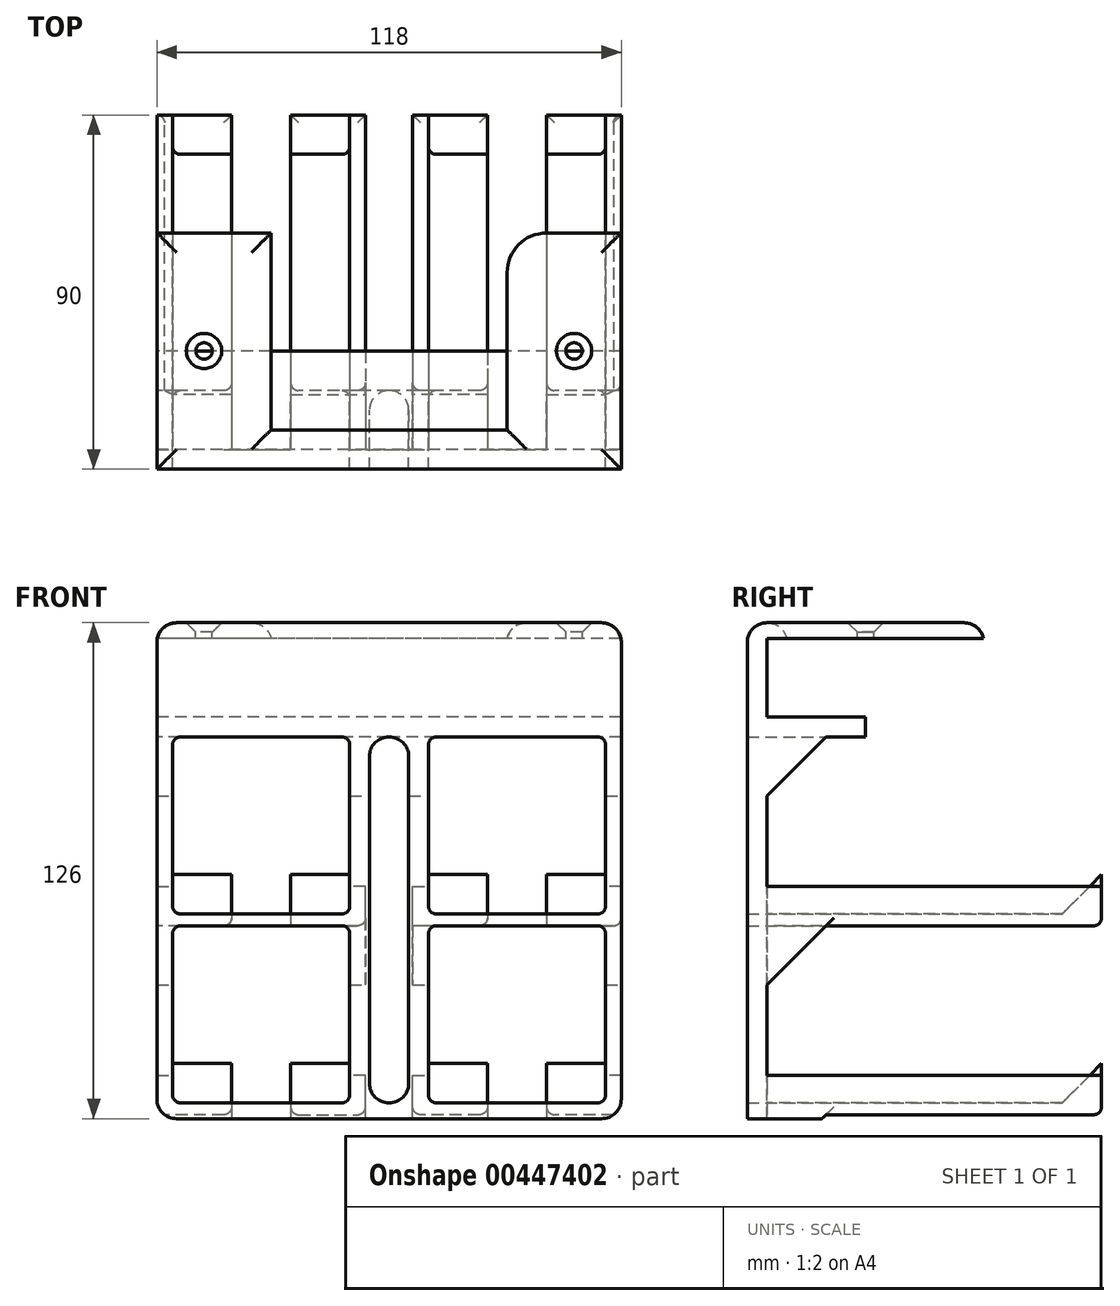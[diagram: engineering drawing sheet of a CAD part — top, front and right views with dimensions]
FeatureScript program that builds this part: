
annotation { "Feature Type Name" : "Feature", "Feature Type Description" : "" }
export const myFeature = defineFeature(function(context is Context, id is Id, definition is map)
    precondition{}
    {
        {
            var Q0;
            Q0=qCreatedBy(makeId("Front.planeOp"),FACE);
            var sketch = newSketch(context, id + "F0", { "sketchPlane" : qUnion([Q0])});
            skLineSegment(sketch, "E0.bottom", {"start": v(-55, -29) * mm, "end": v(-10, -29) * mm});
            skLineSegment(sketch, "E0.top", {"start": v(-55, -74) * mm, "end": v(-10, -74) * mm});
            skLineSegment(sketch, "E0.left", {"start": v(-55, -29) * mm, "end": v(-55, -74) * mm});
            skLineSegment(sketch, "E0.right", {"start": v(-10, -29) * mm, "end": v(-10, -74) * mm});
            skLineSegment(sketch, "E1.MirrorCS", {"start": v(10, -29) * mm, "end": v(10, -74) * mm});
            skLineSegment(sketch, "E2.MirrorCS", {"start": v(55, -29) * mm, "end": v(55, -74) * mm});
            skLineSegment(sketch, "E3.MirrorCS", {"start": v(55, -29) * mm, "end": v(10, -29) * mm});
            skLineSegment(sketch, "E4.MirrorCS", {"start": v(55, -74) * mm, "end": v(10, -74) * mm});
            skLineSegment(sketch, "E5", {"start": v(-55, -75.5) * mm, "end": v(55, -75.5) * mm, "construction": true});
            skLineSegment(sketch, "E6.MirrorCS", {"start": v(-55, -77) * mm, "end": v(-10, -77) * mm});
            skLineSegment(sketch, "E7.MirrorCS", {"start": v(-55, -122) * mm, "end": v(-55, -77) * mm});
            skLineSegment(sketch, "E8.MirrorCS", {"start": v(-55, -122) * mm, "end": v(-10, -122) * mm});
            skLineSegment(sketch, "E9.MirrorCS", {"start": v(-10, -122) * mm, "end": v(-10, -77) * mm});
            skLineSegment(sketch, "E10.MirrorCS", {"start": v(10, -122) * mm, "end": v(10, -77) * mm});
            skLineSegment(sketch, "E11.MirrorCS", {"start": v(55, -122) * mm, "end": v(10, -122) * mm});
            skLineSegment(sketch, "E12.MirrorCS", {"start": v(55, -122) * mm, "end": v(55, -77) * mm});
            skLineSegment(sketch, "E13.MirrorCS", {"start": v(55, -77) * mm, "end": v(10, -77) * mm});
            skLineSegment(sketch, "E14.bottom", {"start": v(-59, 0) * mm, "end": v(59, 0) * mm});
            skLineSegment(sketch, "E14.top", {"start": v(-59, -126) * mm, "end": v(59, -126) * mm});
            skLineSegment(sketch, "E14.left", {"start": v(-59, 0) * mm, "end": v(-59, -126) * mm});
            skLineSegment(sketch, "E14.right", {"start": v(59, 0) * mm, "end": v(59, -126) * mm});
            skLineSegment(sketch, "E15", {"start": v(0, -34) * mm, "end": v(0, -117) * mm, "construction": true});
            skLineSegment(sketch, "E16", {"start": v(0, -117) * mm, "end": v(0, -122) * mm, "construction": true});
            skLineSegment(sketch, "E17", {"start": v(0, -34) * mm, "end": v(0, -29) * mm, "construction": true});
            skArc(sketch, "E18.0.startCap", {"start": v(-5, -34) * mm, "mid": v(0, -29) * mm, "end": v(5, -34) * mm});
            skArc(sketch, "E18.0.endCap", {"start": v(5, -117) * mm, "mid": v(0, -122) * mm, "end": v(-5, -117) * mm});
            skLineSegment(sketch, "E18.0.left", {"start": v(5, -34) * mm, "end": v(5, -117) * mm});
            skLineSegment(sketch, "E18.0.right", {"start": v(-5, -34) * mm, "end": v(-5, -117) * mm});
            skSolve(sketch);
        }
        {
            var Q0;
            Q0=makeQuery(id+"F0.imprint","IMPRINT",FACE,{"disambiguationData":[TD([[makeQuery(id+"F0.imprint","IMPRINT",EDGE,{"derivedFrom":sQuery(id+"F0.wireOp",EDGE,"E0.bottom")}),1.0]])]});
            extrude(context, id + "F1", {"entities" : qUnion([Q0]), "depth" : 5 * mm});
        }
        {
            var Q0;
            Q0=makeQuery(id+"F1.opExtrude","CAP_FACE",FACE,{"disambiguationData":[OSD([sQuery(id+"F0.wireOp",EDGE,"E0.bottom"),sQuery(id+"F0.wireOp",EDGE,"E0.top"),sQuery(id+"F0.wireOp",EDGE,"E0.left"),sQuery(id+"F0.wireOp",EDGE,"E0.right"),sQuery(id+"F0.wireOp",EDGE,"E1.MirrorCS"),sQuery(id+"F0.wireOp",EDGE,"E2.MirrorCS"),sQuery(id+"F0.wireOp",EDGE,"E3.MirrorCS"),sQuery(id+"F0.wireOp",EDGE,"E4.MirrorCS"),sQuery(id+"F0.wireOp",EDGE,"E6.MirrorCS"),sQuery(id+"F0.wireOp",EDGE,"E7.MirrorCS"),sQuery(id+"F0.wireOp",EDGE,"E8.MirrorCS"),sQuery(id+"F0.wireOp",EDGE,"E9.MirrorCS"),sQuery(id+"F0.wireOp",EDGE,"E10.MirrorCS"),sQuery(id+"F0.wireOp",EDGE,"E11.MirrorCS"),sQuery(id+"F0.wireOp",EDGE,"E12.MirrorCS"),sQuery(id+"F0.wireOp",EDGE,"E13.MirrorCS"),sQuery(id+"F0.wireOp",EDGE,"E14.bottom"),sQuery(id+"F0.wireOp",EDGE,"E14.top"),sQuery(id+"F0.wireOp",EDGE,"E14.left"),sQuery(id+"F0.wireOp",EDGE,"E14.right")])],"isStart":true});
            var sketch = newSketch(context, id + "F2", { "sketchPlane" : qUnion([Q0])});
            skLineSegment(sketch, "E19.bottom", {"start": v(-59, 0) * mm, "end": v(59, 0) * mm});
            skLineSegment(sketch, "E19.top", {"start": v(-59, -4) * mm, "end": v(59, -4) * mm});
            skLineSegment(sketch, "E19.left", {"start": v(-59, 0) * mm, "end": v(-59, -4) * mm});
            skLineSegment(sketch, "E19.right", {"start": v(59, 0) * mm, "end": v(59, -4) * mm});
            skSolve(sketch);
        }
        {
            var Q0;
            Q0 = qSketchRegion(id + "F2", true);
            extrude(context, id + "F3", {"entities" : qUnion([Q0]), "operationType" : NewBodyOperationType.ADD, "depth" : 55 * mm});
        }
        {
            var Q0;
            Q0=makeQuery(id+"F1.opExtrude","CAP_FACE",FACE,{"disambiguationData":[OSD([sQuery(id+"F0.wireOp",EDGE,"E0.bottom"),sQuery(id+"F0.wireOp",EDGE,"E0.top"),sQuery(id+"F0.wireOp",EDGE,"E0.left"),sQuery(id+"F0.wireOp",EDGE,"E0.right"),sQuery(id+"F0.wireOp",EDGE,"E1.MirrorCS"),sQuery(id+"F0.wireOp",EDGE,"E2.MirrorCS"),sQuery(id+"F0.wireOp",EDGE,"E3.MirrorCS"),sQuery(id+"F0.wireOp",EDGE,"E4.MirrorCS"),sQuery(id+"F0.wireOp",EDGE,"E6.MirrorCS"),sQuery(id+"F0.wireOp",EDGE,"E7.MirrorCS"),sQuery(id+"F0.wireOp",EDGE,"E8.MirrorCS"),sQuery(id+"F0.wireOp",EDGE,"E9.MirrorCS"),sQuery(id+"F0.wireOp",EDGE,"E10.MirrorCS"),sQuery(id+"F0.wireOp",EDGE,"E11.MirrorCS"),sQuery(id+"F0.wireOp",EDGE,"E12.MirrorCS"),sQuery(id+"F0.wireOp",EDGE,"E13.MirrorCS"),sQuery(id+"F0.wireOp",EDGE,"E14.bottom"),sQuery(id+"F0.wireOp",EDGE,"E14.top"),sQuery(id+"F0.wireOp",EDGE,"E14.left"),sQuery(id+"F0.wireOp",EDGE,"E14.right")])],"isStart":true});
            var sketch = newSketch(context, id + "F4", { "sketchPlane" : qUnion([Q0])});
            skLineSegment(sketch, "E20.bottom", {"start": v(-59, -24) * mm, "end": v(59, -24) * mm});
            skLineSegment(sketch, "E20.top", {"start": v(-59, -29) * mm, "end": v(59, -29) * mm});
            skLineSegment(sketch, "E20.left", {"start": v(-59, -24) * mm, "end": v(-59, -29) * mm});
            skLineSegment(sketch, "E20.right", {"start": v(59, -24) * mm, "end": v(59, -29) * mm});
            skSolve(sketch);
        }
        {
            var Q0;
            Q0=makeQuery(id+"F4.imprint","IMPRINT",FACE,{"disambiguationData":[TD([[makeQuery(id+"F4.imprint","IMPRINT",EDGE,{"derivedFrom":sQuery(id+"F4.wireOp",EDGE,"E20.bottom")}),-1.0]])]});
            extrude(context, id + "F5", {"entities" : qUnion([Q0]), "operationType" : NewBodyOperationType.ADD, "depth" : 25 * mm});
        }
        {
            var Q0;
            {var subQ0=sQuery(id+"F0.wireOp",EDGE,"E14.right");var subQ1=sQuery(id+"F0.wireOp",EDGE,"E14.left");var subQ2=sQuery(id+"F0.wireOp",EDGE,"E14.top");var subQ3=sQuery(id+"F0.wireOp",EDGE,"E13.MirrorCS");var subQ4=sQuery(id+"F0.wireOp",EDGE,"E12.MirrorCS");var subQ5=sQuery(id+"F0.wireOp",EDGE,"E11.MirrorCS");var subQ6=sQuery(id+"F0.wireOp",EDGE,"E10.MirrorCS");var subQ7=sQuery(id+"F0.wireOp",EDGE,"E9.MirrorCS");var subQ8=sQuery(id+"F0.wireOp",EDGE,"E8.MirrorCS");var subQ9=sQuery(id+"F0.wireOp",EDGE,"E0.left");var subQ10=sQuery(id+"F0.wireOp",EDGE,"E0.top");var subQ11=sQuery(id+"F0.wireOp",EDGE,"E0.right");var subQ12=sQuery(id+"F0.wireOp",EDGE,"E0.bottom");var subQ13=sQuery(id+"F0.wireOp",EDGE,"E7.MirrorCS");var subQ14=sQuery(id+"F0.wireOp",EDGE,"E1.MirrorCS");var subQ15=sQuery(id+"F0.wireOp",EDGE,"E2.MirrorCS");var subQ16=sQuery(id+"F0.wireOp",EDGE,"E3.MirrorCS");var subQ17=sQuery(id+"F0.wireOp",EDGE,"E4.MirrorCS");var subQ18=sQuery(id+"F0.wireOp",EDGE,"E6.MirrorCS");Q0=makeQuery(id+"F5.boolean.opBoolean","SPLIT",FACE,{"disambiguationData":[TD([makeQuery(id+"F1.opExtrude","SWEPT_FACE",FACE,{"disambiguationData":[OSD([subQ12])]})])],"derivedFrom":makeQuery(id+"F1.opExtrude","CAP_FACE",FACE,{"disambiguationData":[OSD([subQ12,subQ10,subQ9,subQ11,subQ14,subQ15,subQ16,subQ17,subQ18,subQ13,subQ8,subQ7,subQ6,subQ5,subQ4,subQ3,sQuery(id+"F0.wireOp",EDGE,"E14.bottom"),subQ2,subQ1,subQ0])],"isStart":true})});}
            var sketch = newSketch(context, id + "F6", { "sketchPlane" : qUnion([Q0])});
            skLineSegment(sketch, "E21", {"start": v(-59, -67) * mm, "end": v(-55, -67) * mm});
            skLineSegment(sketch, "E22", {"start": v(-55, -67) * mm, "end": v(-55, -74) * mm});
            skLineSegment(sketch, "E23", {"start": v(-55, -74) * mm, "end": v(-40, -74) * mm});
            skLineSegment(sketch, "E24", {"start": v(-40, -74) * mm, "end": v(-40, -77) * mm});
            skLineSegment(sketch, "E25", {"start": v(-40, -77) * mm, "end": v(-59, -77) * mm});
            skLineSegment(sketch, "E26", {"start": v(-59, -77) * mm, "end": v(-59, -67) * mm});
            skLineSegment(sketch, "E27", {"start": v(-32.5, -74) * mm, "end": v(-32.5, -29) * mm, "construction": true});
            skPoint(sketch, "E27.endSnap0", {"position": v(-32.5, -74) * mm});
            skLineSegment(sketch, "E28", {"start": v(5, -29) * mm, "end": v(0, -130.75) * mm, "construction": true});
            skPoint(sketch, "E28.endSnap0", {"position": v(0, -126) * mm});
            skLineSegment(sketch, "E29.MirrorCS", {"start": v(-25, -74) * mm, "end": v(-25, -77) * mm});
            skLineSegment(sketch, "E30.MirrorCS", {"start": v(-10, -74) * mm, "end": v(-25, -74) * mm});
            skLineSegment(sketch, "E31.MirrorCS", {"start": v(-25, -77) * mm, "end": v(-6, -77) * mm});
            skLineSegment(sketch, "E32.MirrorCS", {"start": v(-6, -77) * mm, "end": v(-6, -67) * mm});
            skLineSegment(sketch, "E33.MirrorCS", {"start": v(-10, -67) * mm, "end": v(-10, -74) * mm});
            skLineSegment(sketch, "E34.MirrorCS", {"start": v(-6, -67) * mm, "end": v(-10, -67) * mm});
            skLineSegment(sketch, "E35.0.1.0", {"start": v(-59, -125) * mm, "end": v(-59, -115) * mm});
            skLineSegment(sketch, "E35.0.1.1", {"start": v(-59, -115) * mm, "end": v(-55, -115) * mm});
            skLineSegment(sketch, "E35.0.1.2", {"start": v(-55, -115) * mm, "end": v(-55, -122) * mm});
            skLineSegment(sketch, "E35.0.1.3", {"start": v(-55, -122) * mm, "end": v(-40, -122) * mm});
            skLineSegment(sketch, "E35.0.1.4", {"start": v(-40, -122) * mm, "end": v(-40, -125) * mm});
            skLineSegment(sketch, "E35.0.1.5", {"start": v(-40, -125) * mm, "end": v(-59, -125) * mm});
            skLineSegment(sketch, "E35.0.1.6", {"start": v(-25, -125) * mm, "end": v(-6, -125) * mm});
            skLineSegment(sketch, "E35.0.1.7", {"start": v(-6, -125) * mm, "end": v(-6, -115) * mm});
            skLineSegment(sketch, "E35.0.1.8", {"start": v(-6, -115) * mm, "end": v(-10, -115) * mm});
            skLineSegment(sketch, "E35.0.1.9", {"start": v(-10, -115) * mm, "end": v(-10, -122) * mm});
            skLineSegment(sketch, "E35.0.1.10", {"start": v(-10, -122) * mm, "end": v(-25, -122) * mm});
            skLineSegment(sketch, "E35.0.1.11", {"start": v(-25, -122) * mm, "end": v(-25, -125) * mm});
            skLineSegment(sketch, "E35.1.0.0", {"start": v(6, -77) * mm, "end": v(6, -67) * mm});
            skLineSegment(sketch, "E35.1.0.1", {"start": v(6, -67) * mm, "end": v(10, -67) * mm});
            skLineSegment(sketch, "E35.1.0.2", {"start": v(10, -67) * mm, "end": v(10, -74) * mm});
            skLineSegment(sketch, "E35.1.0.3", {"start": v(10, -74) * mm, "end": v(25, -74) * mm});
            skLineSegment(sketch, "E35.1.0.4", {"start": v(25, -74) * mm, "end": v(25, -77) * mm});
            skLineSegment(sketch, "E35.1.0.5", {"start": v(25, -77) * mm, "end": v(6, -77) * mm});
            skLineSegment(sketch, "E35.1.0.6", {"start": v(40, -77) * mm, "end": v(59, -77) * mm});
            skLineSegment(sketch, "E35.1.0.7", {"start": v(59, -77) * mm, "end": v(59, -67) * mm});
            skLineSegment(sketch, "E35.1.0.8", {"start": v(59, -67) * mm, "end": v(55, -67) * mm});
            skLineSegment(sketch, "E35.1.0.9", {"start": v(55, -67) * mm, "end": v(55, -74) * mm});
            skLineSegment(sketch, "E35.1.0.10", {"start": v(55, -74) * mm, "end": v(40, -74) * mm});
            skLineSegment(sketch, "E35.1.0.11", {"start": v(40, -74) * mm, "end": v(40, -77) * mm});
            skLineSegment(sketch, "E35.1.1.0", {"start": v(6, -125) * mm, "end": v(6, -115) * mm});
            skLineSegment(sketch, "E35.1.1.1", {"start": v(6, -115) * mm, "end": v(10, -115) * mm});
            skLineSegment(sketch, "E35.1.1.2", {"start": v(10, -115) * mm, "end": v(10, -122) * mm});
            skLineSegment(sketch, "E35.1.1.3", {"start": v(10, -122) * mm, "end": v(25, -122) * mm});
            skLineSegment(sketch, "E35.1.1.4", {"start": v(25, -122) * mm, "end": v(25, -125) * mm});
            skLineSegment(sketch, "E35.1.1.5", {"start": v(25, -125) * mm, "end": v(6, -125) * mm});
            skLineSegment(sketch, "E35.1.1.6", {"start": v(40, -125) * mm, "end": v(59, -125) * mm});
            skLineSegment(sketch, "E35.1.1.7", {"start": v(59, -125) * mm, "end": v(59, -115) * mm});
            skLineSegment(sketch, "E35.1.1.8", {"start": v(59, -115) * mm, "end": v(55, -115) * mm});
            skLineSegment(sketch, "E35.1.1.9", {"start": v(55, -115) * mm, "end": v(55, -122) * mm});
            skLineSegment(sketch, "E35.1.1.10", {"start": v(55, -122) * mm, "end": v(40, -122) * mm});
            skLineSegment(sketch, "E35.1.1.11", {"start": v(40, -122) * mm, "end": v(40, -125) * mm});
            skLineSegment(sketch, "E35.direction1", {"start": v(-59, -77) * mm, "end": v(6, -77) * mm, "construction": true});
            skLineSegment(sketch, "E35.direction2", {"start": v(-59, -77) * mm, "end": v(-59, -125) * mm, "construction": true});
            skSolve(sketch);
        }
        {
            var Q0;
            Q0=makeQuery(id+"F6.imprint","IMPRINT",FACE,{"disambiguationData":[TD([[makeQuery(id+"F6.imprint","IMPRINT",EDGE,{"derivedFrom":sQuery(id+"F6.wireOp",EDGE,"E21")}),-1.0]])]});
            var Q1;
            {var subQ2=sQuery(id+"F6.wireOp",EDGE,"E29.MirrorCS");Q1=makeQuery(id+"F6.imprint","IMPRINT",FACE,{"disambiguationData":[TD([[makeQuery(id+"F6.imprint","IMPRINT",EDGE,{"derivedFrom":subQ2}),1.0]])]});}
            var Q2;
            {var subQ0=sQuery(id+"F6.wireOp",EDGE,"E35.1.0.0");Q2=makeQuery(id+"F6.imprint","IMPRINT",FACE,{"disambiguationData":[TD([[makeQuery(id+"F6.imprint","IMPRINT",EDGE,{"derivedFrom":subQ0}),-1.0]])]});}
            var Q3;
            {var subQ0=sQuery(id+"F6.wireOp",EDGE,"E35.1.0.7");Q3=makeQuery(id+"F6.imprint","IMPRINT",FACE,{"disambiguationData":[TD([[makeQuery(id+"F6.imprint","IMPRINT",EDGE,{"derivedFrom":subQ0}),-1.0]])]});}
            var Q4;
            Q4=makeQuery(id+"F6.imprint","IMPRINT",FACE,{"disambiguationData":[TD([[makeQuery(id+"F6.imprint","IMPRINT",EDGE,{"derivedFrom":sQuery(id+"F6.wireOp",EDGE,"E35.1.1.6")}),1.0]])]});
            var Q5;
            Q5=makeQuery(id+"F6.imprint","IMPRINT",FACE,{"disambiguationData":[TD([[makeQuery(id+"F6.imprint","IMPRINT",EDGE,{"derivedFrom":sQuery(id+"F6.wireOp",EDGE,"E35.1.1.0")}),-1.0]])]});
            var Q6;
            Q6=makeQuery(id+"F6.imprint","IMPRINT",FACE,{"disambiguationData":[TD([[makeQuery(id+"F6.imprint","IMPRINT",EDGE,{"derivedFrom":sQuery(id+"F6.wireOp",EDGE,"E35.0.1.6")}),1.0]])]});
            var Q7;
            Q7=makeQuery(id+"F6.imprint","IMPRINT",FACE,{"disambiguationData":[TD([[makeQuery(id+"F6.imprint","IMPRINT",EDGE,{"derivedFrom":sQuery(id+"F6.wireOp",EDGE,"E35.0.1.0")}),1.0]])]});
            extrude(context, id + "F7", {"entities" : qUnion([Q0, Q1, Q2, Q3, Q4, Q5, Q6, Q7]), "operationType" : NewBodyOperationType.ADD, "depth" : 85 * mm});
        }
        {
            var Q0;
            Q0=makeQuery(id+"F7.boolean.opBoolean","MERGE",FACE,{"derivedFrom":[makeQuery(id+"F1.opExtrude","SWEPT_FACE",FACE,{"disambiguationData":[OSD([sQuery(id+"F0.wireOp",EDGE,"E4.MirrorCS")])]}),makeQuery(id+"F7.opExtrude","SWEPT_FACE",FACE,{"disambiguationData":[OSD([sQuery(id+"F6.wireOp",EDGE,"E23")])]}),makeQuery(id+"F7.opExtrude","SWEPT_FACE",FACE,{"disambiguationData":[OSD([sQuery(id+"F6.wireOp",EDGE,"E30.MirrorCS")])]})]});
            var sketch = newSketch(context, id + "F8", { "sketchPlane" : qUnion([Q0])});
            skLineSegment(sketch, "E36.bottom", {"start": v(55, 75) * mm, "end": v(40, 75) * mm});
            skLineSegment(sketch, "E36.top", {"start": v(55, 85) * mm, "end": v(40, 85) * mm});
            skLineSegment(sketch, "E36.left", {"start": v(55, 75) * mm, "end": v(55, 85) * mm});
            skLineSegment(sketch, "E36.right", {"start": v(40, 75) * mm, "end": v(40, 85) * mm});
            skLineSegment(sketch, "E37.bottom", {"start": v(25, 85) * mm, "end": v(10, 85) * mm});
            skLineSegment(sketch, "E37.top", {"start": v(25, 75) * mm, "end": v(10, 75) * mm});
            skLineSegment(sketch, "E37.left", {"start": v(25, 85) * mm, "end": v(25, 75) * mm});
            skLineSegment(sketch, "E37.right", {"start": v(10, 85) * mm, "end": v(10, 75) * mm});
            skLineSegment(sketch, "E38.0.0", {"start": v(-25, 0) * mm, "end": v(-40, 0) * mm});
            skLineSegment(sketch, "E38.0.1", {"start": v(-40, 0) * mm, "end": v(-40, 85) * mm});
            skLineSegment(sketch, "E38.0.2", {"start": v(-40, 85) * mm, "end": v(-55, 85) * mm});
            skLineSegment(sketch, "E38.0.3", {"start": v(-55, 85) * mm, "end": v(-55, -5) * mm});
            skLineSegment(sketch, "E38.0.4", {"start": v(-55, -5) * mm, "end": v(-10, -5) * mm});
            skLineSegment(sketch, "E38.0.5", {"start": v(-10, -5) * mm, "end": v(-10, 85) * mm});
            skLineSegment(sketch, "E38.0.6", {"start": v(-10, 85) * mm, "end": v(-25, 85) * mm});
            skLineSegment(sketch, "E38.0.7", {"start": v(-25, 85) * mm, "end": v(-25, 0) * mm});
            skLineSegment(sketch, "E39.bottom", {"start": v(-10, 75) * mm, "end": v(-25, 75) * mm});
            skLineSegment(sketch, "E39.left", {"start": v(-10, 75) * mm, "end": v(-10, 85) * mm});
            skLineSegment(sketch, "E39.right", {"start": v(-25, 75) * mm, "end": v(-25, 85) * mm});
            skLineSegment(sketch, "E40.bottom", {"start": v(-40, 75) * mm, "end": v(-55, 75) * mm});
            skLineSegment(sketch, "E40.left", {"start": v(-40, 75) * mm, "end": v(-40, 85) * mm});
            skLineSegment(sketch, "E40.right", {"start": v(-55, 75) * mm, "end": v(-55, 85) * mm});
            skSolve(sketch);
        }
        {
            var Q0;
            Q0=makeQuery(id+"F7.boolean.opBoolean","MERGE",FACE,{"derivedFrom":[makeQuery(id+"F1.opExtrude","SWEPT_FACE",FACE,{"disambiguationData":[OSD([sQuery(id+"F0.wireOp",EDGE,"E11.MirrorCS")])]}),makeQuery(id+"F7.opExtrude","SWEPT_FACE",FACE,{"disambiguationData":[OSD([sQuery(id+"F6.wireOp",EDGE,"E35.0.1.3")])]}),makeQuery(id+"F7.opExtrude","SWEPT_FACE",FACE,{"disambiguationData":[OSD([sQuery(id+"F6.wireOp",EDGE,"E35.0.1.10")])]})]});
            var sketch = newSketch(context, id + "F9", { "sketchPlane" : qUnion([Q0])});
            skLineSegment(sketch, "E41.bottom", {"start": v(55, 85) * mm, "end": v(40, 85) * mm});
            skLineSegment(sketch, "E41.top", {"start": v(55, 75) * mm, "end": v(40, 75) * mm});
            skLineSegment(sketch, "E41.left", {"start": v(55, 85) * mm, "end": v(55, 75) * mm});
            skLineSegment(sketch, "E41.right", {"start": v(40, 85) * mm, "end": v(40, 75) * mm});
            skLineSegment(sketch, "E42.bottom", {"start": v(25, 75) * mm, "end": v(10, 75) * mm});
            skLineSegment(sketch, "E42.top", {"start": v(25, 85) * mm, "end": v(10, 85) * mm});
            skLineSegment(sketch, "E42.left", {"start": v(25, 75) * mm, "end": v(25, 85) * mm});
            skLineSegment(sketch, "E42.right", {"start": v(10, 75) * mm, "end": v(10, 85) * mm});
            skLineSegment(sketch, "E43.0.0", {"start": v(-25, 0) * mm, "end": v(-40, 0) * mm});
            skLineSegment(sketch, "E43.0.1", {"start": v(-40, 0) * mm, "end": v(-40, 85) * mm});
            skLineSegment(sketch, "E43.0.2", {"start": v(-40, 85) * mm, "end": v(-55, 85) * mm});
            skLineSegment(sketch, "E43.0.3", {"start": v(-55, 85) * mm, "end": v(-55, -5) * mm});
            skLineSegment(sketch, "E43.0.4", {"start": v(-55, -5) * mm, "end": v(-10, -5) * mm});
            skLineSegment(sketch, "E43.0.5", {"start": v(-10, -5) * mm, "end": v(-10, 85) * mm});
            skLineSegment(sketch, "E43.0.6", {"start": v(-10, 85) * mm, "end": v(-25, 85) * mm});
            skLineSegment(sketch, "E43.0.7", {"start": v(-25, 85) * mm, "end": v(-25, 0) * mm});
            skLineSegment(sketch, "E44.bottom", {"start": v(-10, 75) * mm, "end": v(-25, 75) * mm});
            skLineSegment(sketch, "E44.left", {"start": v(-10, 75) * mm, "end": v(-10, 85) * mm});
            skLineSegment(sketch, "E44.right", {"start": v(-25, 75) * mm, "end": v(-25, 85) * mm});
            skLineSegment(sketch, "E45.bottom", {"start": v(-40, 75) * mm, "end": v(-55, 75) * mm});
            skLineSegment(sketch, "E45.left", {"start": v(-40, 75) * mm, "end": v(-40, 85) * mm});
            skLineSegment(sketch, "E45.right", {"start": v(-55, 75) * mm, "end": v(-55, 85) * mm});
            skSolve(sketch);
        }
        {
            var Q0;
            Q0=makeQuery(id+"F8.imprint","IMPRINT",FACE,{"disambiguationData":[TD([[makeQuery(id+"F8.imprint","IMPRINT",EDGE,{"derivedFrom":sQuery(id+"F8.wireOp",EDGE,"E36.bottom")}),-1.0]])]});
            var Q1;
            Q1=makeQuery(id+"F8.imprint","IMPRINT",FACE,{"disambiguationData":[TD([[makeQuery(id+"F8.imprint","IMPRINT",EDGE,{"derivedFrom":sQuery(id+"F8.wireOp",EDGE,"E37.bottom")}),1.0]])]});
            var Q2;
            Q2=makeQuery(id+"F8.imprint","IMPRINT",FACE,{"disambiguationData":[TD([[makeQuery(id+"F8.imprint","IMPRINT",EDGE,{"derivedFrom":sQuery(id+"F8.wireOp",EDGE,"E39.bottom")}),-1.0]])]});
            var Q3;
            Q3=makeQuery(id+"F8.imprint","IMPRINT",FACE,{"disambiguationData":[TD([[makeQuery(id+"F8.imprint","IMPRINT",EDGE,{"derivedFrom":sQuery(id+"F8.wireOp",EDGE,"E40.bottom")}),-1.0]])]});
            var Q4;
            Q4=makeQuery(id+"F9.imprint","IMPRINT",FACE,{"disambiguationData":[TD([[makeQuery(id+"F9.imprint","IMPRINT",EDGE,{"derivedFrom":sQuery(id+"F9.wireOp",EDGE,"E41.bottom")}),1.0]])]});
            var Q5;
            Q5=makeQuery(id+"F9.imprint","IMPRINT",FACE,{"disambiguationData":[TD([[makeQuery(id+"F9.imprint","IMPRINT",EDGE,{"derivedFrom":sQuery(id+"F9.wireOp",EDGE,"E42.bottom")}),-1.0]])]});
            var Q6;
            Q6=makeQuery(id+"F9.imprint","IMPRINT",FACE,{"disambiguationData":[TD([[makeQuery(id+"F9.imprint","IMPRINT",EDGE,{"derivedFrom":sQuery(id+"F9.wireOp",EDGE,"E44.bottom")}),-1.0]])]});
            var Q7;
            Q7=makeQuery(id+"F9.imprint","IMPRINT",FACE,{"disambiguationData":[TD([[makeQuery(id+"F9.imprint","IMPRINT",EDGE,{"derivedFrom":sQuery(id+"F9.wireOp",EDGE,"E45.bottom")}),-1.0]])]});
            extrude(context, id + "F10", {"entities" : qUnion([Q0, Q1, Q2, Q3, Q4, Q5, Q6, Q7]), "operationType" : NewBodyOperationType.ADD, "depth" : 10 * mm});
        }
        {
            var Q0;
            Q0=makeQuery(id+"F10.opExtrude","CAP_EDGE",EDGE,{"disambiguationData":[OSD([sQuery(id+"F8.wireOp",EDGE,"E40.bottom")])],"isStart":false});
            var Q1;
            Q1=makeQuery(id+"F10.opExtrude","CAP_EDGE",EDGE,{"disambiguationData":[OSD([sQuery(id+"F8.wireOp",EDGE,"E39.bottom")])],"isStart":false});
            var Q2;
            Q2=makeQuery(id+"F10.opExtrude","CAP_EDGE",EDGE,{"disambiguationData":[OSD([sQuery(id+"F8.wireOp",EDGE,"E37.top")])],"isStart":false});
            var Q3;
            Q3=makeQuery(id+"F10.opExtrude","CAP_EDGE",EDGE,{"disambiguationData":[OSD([sQuery(id+"F8.wireOp",EDGE,"E36.bottom")])],"isStart":false});
            var Q4;
            Q4=makeQuery(id+"F10.opExtrude","CAP_EDGE",EDGE,{"disambiguationData":[OSD([sQuery(id+"F9.wireOp",EDGE,"E45.bottom")])],"isStart":false});
            var Q5;
            Q5=makeQuery(id+"F10.opExtrude","CAP_EDGE",EDGE,{"disambiguationData":[OSD([sQuery(id+"F9.wireOp",EDGE,"E44.bottom")])],"isStart":false});
            var Q6;
            Q6=makeQuery(id+"F10.opExtrude","CAP_EDGE",EDGE,{"disambiguationData":[OSD([sQuery(id+"F9.wireOp",EDGE,"E42.bottom")])],"isStart":false});
            var Q7;
            Q7=makeQuery(id+"F10.opExtrude","CAP_EDGE",EDGE,{"disambiguationData":[OSD([sQuery(id+"F9.wireOp",EDGE,"E41.top")])],"isStart":false});
            chamfer(context, id + "F11", {"entities" : qUnion([Q0, Q1, Q2, Q3, Q4, Q5, Q6, Q7]), "width" : 10 * mm, "tangentPropagation" : true});
        }
        {
            var Q0;
            {var subQ1=sQuery(id+"F0.wireOp",EDGE,"E0.left");var subQ4=sQuery(id+"F4.wireOp",EDGE,"E20.top");Q0=makeQuery(id+"F5.boolean.opBoolean","SPLIT",EDGE,{"disambiguationData":[TD([makeQuery(id+"F1.opExtrude","SWEPT_FACE",FACE,{"disambiguationData":[OSD([subQ1])]})])],"derivedFrom":makeQuery(id+"F5.opExtrude","CAP_EDGE",EDGE,{"disambiguationData":[OSD([subQ4])],"isStart":true})});}
            var Q1;
            {var subQ2=sQuery(id+"F0.wireOp",EDGE,"E0.right");var subQ4=sQuery(id+"F4.wireOp",EDGE,"E20.top");Q1=makeQuery(id+"F5.boolean.opBoolean","SPLIT",EDGE,{"disambiguationData":[TD([makeQuery(id+"F1.opExtrude","SWEPT_FACE",FACE,{"disambiguationData":[OSD([subQ2])]})])],"derivedFrom":makeQuery(id+"F5.opExtrude","CAP_EDGE",EDGE,{"disambiguationData":[OSD([subQ4])],"isStart":true})});}
            var Q2;
            {var subQ1=sQuery(id+"F0.wireOp",EDGE,"E1.MirrorCS");var subQ4=sQuery(id+"F4.wireOp",EDGE,"E20.top");Q2=makeQuery(id+"F5.boolean.opBoolean","SPLIT",EDGE,{"disambiguationData":[TD([makeQuery(id+"F1.opExtrude","SWEPT_FACE",FACE,{"disambiguationData":[OSD([subQ1])]})])],"derivedFrom":makeQuery(id+"F5.opExtrude","CAP_EDGE",EDGE,{"disambiguationData":[OSD([subQ4])],"isStart":true})});}
            var Q3;
            {var subQ1=sQuery(id+"F0.wireOp",EDGE,"E2.MirrorCS");var subQ4=sQuery(id+"F4.wireOp",EDGE,"E20.top");Q3=makeQuery(id+"F5.boolean.opBoolean","SPLIT",EDGE,{"disambiguationData":[TD([makeQuery(id+"F1.opExtrude","SWEPT_FACE",FACE,{"disambiguationData":[OSD([subQ1])]})])],"derivedFrom":makeQuery(id+"F5.opExtrude","CAP_EDGE",EDGE,{"disambiguationData":[OSD([subQ4])],"isStart":true})});}
            var Q4;
            Q4=makeQuery(id+"F7.opExtrude","CAP_EDGE",EDGE,{"disambiguationData":[OSD([sQuery(id+"F6.wireOp",EDGE,"E25")])],"isStart":true});
            var Q5;
            Q5=makeQuery(id+"F7.opExtrude","CAP_EDGE",EDGE,{"disambiguationData":[OSD([sQuery(id+"F6.wireOp",EDGE,"E31.MirrorCS")])],"isStart":true});
            var Q6;
            Q6=makeQuery(id+"F7.opExtrude","CAP_EDGE",EDGE,{"disambiguationData":[OSD([sQuery(id+"F6.wireOp",EDGE,"E35.1.0.5")])],"isStart":true});
            var Q7;
            Q7=makeQuery(id+"F7.opExtrude","CAP_EDGE",EDGE,{"disambiguationData":[OSD([sQuery(id+"F6.wireOp",EDGE,"E35.0.1.5")])],"isStart":true});
            var Q8;
            Q8=makeQuery(id+"F7.opExtrude","CAP_EDGE",EDGE,{"disambiguationData":[OSD([sQuery(id+"F6.wireOp",EDGE,"E35.0.1.6")])],"isStart":true});
            var Q9;
            Q9=makeQuery(id+"F7.opExtrude","CAP_EDGE",EDGE,{"disambiguationData":[OSD([sQuery(id+"F6.wireOp",EDGE,"E35.1.1.5")])],"isStart":true});
            var Q10;
            Q10=makeQuery(id+"F7.opExtrude","CAP_EDGE",EDGE,{"disambiguationData":[OSD([sQuery(id+"F6.wireOp",EDGE,"E35.1.1.6")])],"isStart":true});
            var Q11;
            Q11=makeQuery(id+"F7.opExtrude","CAP_EDGE",EDGE,{"disambiguationData":[OSD([sQuery(id+"F6.wireOp",EDGE,"E35.1.0.6")])],"isStart":true});
            chamfer(context, id + "F12", {"entities" : qUnion([Q0, Q1, Q2, Q3, Q4, Q5, Q6, Q7, Q8, Q9, Q10, Q11]), "width" : 15 * mm});
        }
        {
            var Q0;
            Q0=makeQuery(id+"F3.boolean.opBoolean","MERGE",EDGE,{"derivedFrom":[makeQuery(id+"F1.opExtrude","SWEPT_EDGE",EDGE,{"disambiguationData":[OSD([sQuery(id+"F0.wireOp",EDGE,"E14.bottom"),sQuery(id+"F0.wireOp",EDGE,"E14.left")])]}),makeQuery(id+"F3.opExtrude","SWEPT_EDGE",EDGE,{"disambiguationData":[OSD([sQuery(id+"F2.wireOp",EDGE,"E19.bottom"),sQuery(id+"F2.wireOp",EDGE,"E19.right")])]})]});
            var Q1;
            Q1=makeQuery(id+"F3.boolean.opBoolean","MERGE",EDGE,{"derivedFrom":[makeQuery(id+"F1.opExtrude","SWEPT_EDGE",EDGE,{"disambiguationData":[OSD([sQuery(id+"F0.wireOp",EDGE,"E14.bottom"),sQuery(id+"F0.wireOp",EDGE,"E14.right")])]}),makeQuery(id+"F3.opExtrude","SWEPT_EDGE",EDGE,{"disambiguationData":[OSD([sQuery(id+"F2.wireOp",EDGE,"E19.bottom"),sQuery(id+"F2.wireOp",EDGE,"E19.left")])]})]});
            var Q2;
            Q2=makeQuery(id+"F1.opExtrude","SWEPT_EDGE",EDGE,{"disambiguationData":[OSD([sQuery(id+"F0.wireOp",EDGE,"E14.top"),sQuery(id+"F0.wireOp",EDGE,"E14.right")])]});
            var Q3;
            Q3=makeQuery(id+"F1.opExtrude","SWEPT_EDGE",EDGE,{"disambiguationData":[OSD([sQuery(id+"F0.wireOp",EDGE,"E14.top"),sQuery(id+"F0.wireOp",EDGE,"E14.left")])]});
            var Q4;
            Q4=makeQuery(id+"F1.opExtrude","CAP_EDGE",EDGE,{"disambiguationData":[OSD([sQuery(id+"F0.wireOp",EDGE,"E14.bottom")])],"isStart":false});
            fillet(context, id + "F13", {"entities" : qUnion([Q0, Q1, Q2, Q3, Q4]), "radius" : 5 * mm, "tangentPropagation" : true, "allowEdgeOverflow" : false});
        }
        {
            var Q0;
            Q0=makeQuery(id+"F1.opExtrude","SWEPT_EDGE",EDGE,{"disambiguationData":[OSD([sQuery(id+"F0.wireOp",EDGE,"E0.bottom"),sQuery(id+"F0.wireOp",EDGE,"E0.left")])]});
            var Q1;
            Q1=makeQuery(id+"F1.opExtrude","SWEPT_EDGE",EDGE,{"disambiguationData":[OSD([sQuery(id+"F0.wireOp",EDGE,"E1.MirrorCS"),sQuery(id+"F0.wireOp",EDGE,"E3.MirrorCS")])]});
            var Q2;
            Q2=makeQuery(id+"F1.opExtrude","SWEPT_EDGE",EDGE,{"disambiguationData":[OSD([sQuery(id+"F0.wireOp",EDGE,"E0.bottom"),sQuery(id+"F0.wireOp",EDGE,"E0.right")])]});
            var Q3;
            Q3=makeQuery(id+"F1.opExtrude","SWEPT_EDGE",EDGE,{"disambiguationData":[OSD([sQuery(id+"F0.wireOp",EDGE,"E2.MirrorCS"),sQuery(id+"F0.wireOp",EDGE,"E3.MirrorCS")])]});
            var Q4;
            Q4=makeQuery(id+"F7.boolean.opBoolean","MERGE",EDGE,{"derivedFrom":[makeQuery(id+"F1.opExtrude","SWEPT_EDGE",EDGE,{"disambiguationData":[OSD([sQuery(id+"F0.wireOp",EDGE,"E2.MirrorCS"),sQuery(id+"F0.wireOp",EDGE,"E4.MirrorCS")])]}),makeQuery(id+"F7.opExtrude","SWEPT_EDGE",EDGE,{"disambiguationData":[OSD([sQuery(id+"F6.wireOp",EDGE,"E22"),sQuery(id+"F6.wireOp",EDGE,"E23")])]})]});
            var Q5;
            Q5=makeQuery(id+"F7.boolean.opBoolean","MERGE",EDGE,{"derivedFrom":[makeQuery(id+"F1.opExtrude","SWEPT_EDGE",EDGE,{"disambiguationData":[OSD([sQuery(id+"F0.wireOp",EDGE,"E1.MirrorCS"),sQuery(id+"F0.wireOp",EDGE,"E4.MirrorCS")])]}),makeQuery(id+"F7.opExtrude","SWEPT_EDGE",EDGE,{"disambiguationData":[OSD([sQuery(id+"F6.wireOp",EDGE,"E30.MirrorCS"),sQuery(id+"F6.wireOp",EDGE,"E33.MirrorCS")])]})]});
            var Q6;
            Q6=makeQuery(id+"F7.boolean.opBoolean","MERGE",EDGE,{"derivedFrom":[makeQuery(id+"F1.opExtrude","SWEPT_EDGE",EDGE,{"disambiguationData":[OSD([sQuery(id+"F0.wireOp",EDGE,"E0.top"),sQuery(id+"F0.wireOp",EDGE,"E0.right")])]}),makeQuery(id+"F7.opExtrude","SWEPT_EDGE",EDGE,{"disambiguationData":[OSD([sQuery(id+"F6.wireOp",EDGE,"E35.1.0.2"),sQuery(id+"F6.wireOp",EDGE,"E35.1.0.3")])]})]});
            var Q7;
            Q7=makeQuery(id+"F7.boolean.opBoolean","MERGE",EDGE,{"derivedFrom":[makeQuery(id+"F1.opExtrude","SWEPT_EDGE",EDGE,{"disambiguationData":[OSD([sQuery(id+"F0.wireOp",EDGE,"E0.top"),sQuery(id+"F0.wireOp",EDGE,"E0.left")])]}),makeQuery(id+"F7.opExtrude","SWEPT_EDGE",EDGE,{"disambiguationData":[OSD([sQuery(id+"F6.wireOp",EDGE,"E35.1.0.9"),sQuery(id+"F6.wireOp",EDGE,"E35.1.0.10")])]})]});
            var Q8;
            Q8=makeQuery(id+"F1.opExtrude","SWEPT_EDGE",EDGE,{"disambiguationData":[OSD([sQuery(id+"F0.wireOp",EDGE,"E6.MirrorCS"),sQuery(id+"F0.wireOp",EDGE,"E7.MirrorCS")])]});
            var Q9;
            Q9=makeQuery(id+"F1.opExtrude","SWEPT_EDGE",EDGE,{"disambiguationData":[OSD([sQuery(id+"F0.wireOp",EDGE,"E6.MirrorCS"),sQuery(id+"F0.wireOp",EDGE,"E9.MirrorCS")])]});
            var Q10;
            Q10=makeQuery(id+"F1.opExtrude","SWEPT_EDGE",EDGE,{"disambiguationData":[OSD([sQuery(id+"F0.wireOp",EDGE,"E12.MirrorCS"),sQuery(id+"F0.wireOp",EDGE,"E13.MirrorCS")])]});
            var Q11;
            Q11=makeQuery(id+"F1.opExtrude","SWEPT_EDGE",EDGE,{"disambiguationData":[OSD([sQuery(id+"F0.wireOp",EDGE,"E10.MirrorCS"),sQuery(id+"F0.wireOp",EDGE,"E13.MirrorCS")])]});
            var Q12;
            Q12=makeQuery(id+"F7.boolean.opBoolean","MERGE",EDGE,{"derivedFrom":[makeQuery(id+"F1.opExtrude","SWEPT_EDGE",EDGE,{"disambiguationData":[OSD([sQuery(id+"F0.wireOp",EDGE,"E7.MirrorCS"),sQuery(id+"F0.wireOp",EDGE,"E8.MirrorCS")])]}),makeQuery(id+"F7.opExtrude","SWEPT_EDGE",EDGE,{"disambiguationData":[OSD([sQuery(id+"F6.wireOp",EDGE,"E35.1.1.9"),sQuery(id+"F6.wireOp",EDGE,"E35.1.1.10")])]})]});
            var Q13;
            Q13=makeQuery(id+"F7.boolean.opBoolean","MERGE",EDGE,{"derivedFrom":[makeQuery(id+"F1.opExtrude","SWEPT_EDGE",EDGE,{"disambiguationData":[OSD([sQuery(id+"F0.wireOp",EDGE,"E10.MirrorCS"),sQuery(id+"F0.wireOp",EDGE,"E11.MirrorCS")])]}),makeQuery(id+"F7.opExtrude","SWEPT_EDGE",EDGE,{"disambiguationData":[OSD([sQuery(id+"F6.wireOp",EDGE,"E35.0.1.9"),sQuery(id+"F6.wireOp",EDGE,"E35.0.1.10")])]})]});
            var Q14;
            Q14=makeQuery(id+"F7.boolean.opBoolean","MERGE",EDGE,{"derivedFrom":[makeQuery(id+"F1.opExtrude","SWEPT_EDGE",EDGE,{"disambiguationData":[OSD([sQuery(id+"F0.wireOp",EDGE,"E8.MirrorCS"),sQuery(id+"F0.wireOp",EDGE,"E9.MirrorCS")])]}),makeQuery(id+"F7.opExtrude","SWEPT_EDGE",EDGE,{"disambiguationData":[OSD([sQuery(id+"F6.wireOp",EDGE,"E35.1.1.2"),sQuery(id+"F6.wireOp",EDGE,"E35.1.1.3")])]})]});
            var Q15;
            Q15=makeQuery(id+"F7.boolean.opBoolean","MERGE",EDGE,{"derivedFrom":[makeQuery(id+"F1.opExtrude","SWEPT_EDGE",EDGE,{"disambiguationData":[OSD([sQuery(id+"F0.wireOp",EDGE,"E11.MirrorCS"),sQuery(id+"F0.wireOp",EDGE,"E12.MirrorCS")])]}),makeQuery(id+"F7.opExtrude","SWEPT_EDGE",EDGE,{"disambiguationData":[OSD([sQuery(id+"F6.wireOp",EDGE,"E35.0.1.2"),sQuery(id+"F6.wireOp",EDGE,"E35.0.1.3")])]})]});
            var Q16;
            Q16=makeQuery(id+"F7.opExtrude","CAP_EDGE",EDGE,{"disambiguationData":[OSD([sQuery(id+"F6.wireOp",EDGE,"E35.0.1.5")])],"isStart":false});
            var Q17;
            Q17=makeQuery(id+"F7.opExtrude","CAP_EDGE",EDGE,{"disambiguationData":[OSD([sQuery(id+"F6.wireOp",EDGE,"E35.0.1.6")])],"isStart":false});
            var Q18;
            Q18=makeQuery(id+"F7.opExtrude","CAP_EDGE",EDGE,{"disambiguationData":[OSD([sQuery(id+"F6.wireOp",EDGE,"E35.1.1.5")])],"isStart":false});
            var Q19;
            Q19=makeQuery(id+"F7.opExtrude","CAP_EDGE",EDGE,{"disambiguationData":[OSD([sQuery(id+"F6.wireOp",EDGE,"E35.1.1.6")])],"isStart":false});
            var Q20;
            Q20=makeQuery(id+"F7.opExtrude","CAP_EDGE",EDGE,{"disambiguationData":[OSD([sQuery(id+"F6.wireOp",EDGE,"E35.1.0.6")])],"isStart":false});
            var Q21;
            Q21=makeQuery(id+"F7.opExtrude","CAP_EDGE",EDGE,{"disambiguationData":[OSD([sQuery(id+"F6.wireOp",EDGE,"E35.1.0.5")])],"isStart":false});
            var Q22;
            Q22=makeQuery(id+"F7.opExtrude","CAP_EDGE",EDGE,{"disambiguationData":[OSD([sQuery(id+"F6.wireOp",EDGE,"E31.MirrorCS")])],"isStart":false});
            var Q23;
            Q23=makeQuery(id+"F7.opExtrude","CAP_EDGE",EDGE,{"disambiguationData":[OSD([sQuery(id+"F6.wireOp",EDGE,"E25")])],"isStart":false});
            var Q24;
            Q24=makeQuery(id+"F7.opExtrude","SWEPT_EDGE",EDGE,{"disambiguationData":[OSD([sQuery(id+"F6.wireOp",EDGE,"E35.0.1.4"),sQuery(id+"F6.wireOp",EDGE,"E35.0.1.5")])]});
            var Q25;
            Q25=makeQuery(id+"F7.opExtrude","SWEPT_EDGE",EDGE,{"disambiguationData":[OSD([sQuery(id+"F6.wireOp",EDGE,"E35.0.1.6"),sQuery(id+"F6.wireOp",EDGE,"E35.0.1.7")])]});
            var Q26;
            Q26=makeQuery(id+"F7.opExtrude","SWEPT_EDGE",EDGE,{"disambiguationData":[OSD([sQuery(id+"F6.wireOp",EDGE,"E35.1.1.4"),sQuery(id+"F6.wireOp",EDGE,"E35.1.1.5")])]});
            var Q27;
            Q27=makeQuery(id+"F7.opExtrude","SWEPT_EDGE",EDGE,{"disambiguationData":[OSD([sQuery(id+"F6.wireOp",EDGE,"E35.1.1.6"),sQuery(id+"F6.wireOp",EDGE,"E35.1.1.11")])]});
            var Q28;
            Q28=makeQuery(id+"F7.opExtrude","SWEPT_EDGE",EDGE,{"disambiguationData":[OSD([sQuery(id+"F6.wireOp",EDGE,"E35.1.1.0"),sQuery(id+"F6.wireOp",EDGE,"E35.1.1.5")])]});
            var Q29;
            Q29=makeQuery(id+"F7.opExtrude","SWEPT_EDGE",EDGE,{"disambiguationData":[OSD([sQuery(id+"F6.wireOp",EDGE,"E35.0.1.6"),sQuery(id+"F6.wireOp",EDGE,"E35.0.1.11")])]});
            var Q30;
            Q30=makeQuery(id+"F7.opExtrude","SWEPT_EDGE",EDGE,{"disambiguationData":[OSD([sQuery(id+"F0.wireOp",EDGE,"E6.MirrorCS"),sQuery(id+"F6.wireOp",EDGE,"E35.1.0.6"),sQuery(id+"F6.wireOp",EDGE,"E35.1.0.11")])]});
            var Q31;
            Q31=makeQuery(id+"F7.opExtrude","SWEPT_EDGE",EDGE,{"disambiguationData":[OSD([sQuery(id+"F6.wireOp",EDGE,"E35.1.0.0"),sQuery(id+"F6.wireOp",EDGE,"E35.1.0.5")])]});
            var Q32;
            Q32=makeQuery(id+"F7.opExtrude","SWEPT_EDGE",EDGE,{"disambiguationData":[OSD([sQuery(id+"F0.wireOp",EDGE,"E13.MirrorCS"),sQuery(id+"F6.wireOp",EDGE,"E29.MirrorCS"),sQuery(id+"F6.wireOp",EDGE,"E31.MirrorCS")])]});
            var Q33;
            Q33=makeQuery(id+"F7.opExtrude","SWEPT_EDGE",EDGE,{"disambiguationData":[OSD([sQuery(id+"F0.wireOp",EDGE,"E14.right"),sQuery(id+"F6.wireOp",EDGE,"E25"),sQuery(id+"F6.wireOp",EDGE,"E26")])]});
            fillet(context, id + "F14", {"entities" : qUnion([Q0, Q1, Q2, Q3, Q4, Q5, Q6, Q7, Q8, Q9, Q10, Q11, Q12, Q13, Q14, Q15, Q16, Q17, Q18, Q19, Q20, Q21, Q22, Q23, Q24, Q25, Q26, Q27, Q28, Q29, Q30, Q31, Q32, Q33]), "radius" : 2 * mm, "tangentPropagation" : true, "allowEdgeOverflow" : false});
        }
        {
            var Q0;
            Q0=makeQuery(id+"F3.boolean.opBoolean","MERGE",FACE,{"derivedFrom":[makeQuery(id+"F1.opExtrude","SWEPT_FACE",FACE,{"disambiguationData":[OSD([sQuery(id+"F0.wireOp",EDGE,"E14.bottom")])]}),makeQuery(id+"F3.opExtrude","SWEPT_FACE",FACE,{"disambiguationData":[OSD([sQuery(id+"F2.wireOp",EDGE,"E19.bottom")])]})]});
            var sketch = newSketch(context, id + "F15", { "sketchPlane" : qUnion([Q0])});
            skLineSegment(sketch, "E46.bottom", {"start": v(-30, 55) * mm, "end": v(30, 55) * mm});
            skLineSegment(sketch, "E46.top", {"start": v(-30, 5) * mm, "end": v(30, 5) * mm});
            skLineSegment(sketch, "E46.left", {"start": v(-30, 55) * mm, "end": v(-30, 5) * mm});
            skLineSegment(sketch, "E46.right", {"start": v(30, 55) * mm, "end": v(30, 5) * mm});
            skSolve(sketch);
        }
        {
            var Q0;
            Q0=makeQuery(id+"F15.imprint","IMPRINT",FACE,{"disambiguationData":[TD([[makeQuery(id+"F15.imprint","IMPRINT",EDGE,{"derivedFrom":sQuery(id+"F15.wireOp",EDGE,"E46.bottom")}),-1.0]])]});
            extrude(context, id + "F16", {"entities" : qUnion([Q0]), "operationType" : NewBodyOperationType.REMOVE, "endBound" : BoundingType.UP_TO_NEXT, "oppositeDirection" : true, "depth" : 25 * mm});
        }
        {
            var Q0;
            Q0=makeQuery(id+"F16.boolean.opBoolean","COPY",EDGE,{"derivedFrom":makeQuery(id+"F16.opExtrude","SWEPT_EDGE",EDGE,{"disambiguationData":[OSD([sQuery(id+"F2.wireOp",EDGE,"E19.bottom"),sQuery(id+"F15.wireOp",EDGE,"E46.bottom"),sQuery(id+"F15.wireOp",EDGE,"E46.right")])]})});
            var Q1;
            Q1=makeQuery(id+"F16.boolean.opBoolean","COPY",EDGE,{"derivedFrom":makeQuery(id+"F16.opExtrude","SWEPT_EDGE",EDGE,{"disambiguationData":[OSD([sQuery(id+"F2.wireOp",EDGE,"E19.bottom"),sQuery(id+"F15.wireOp",EDGE,"E46.bottom"),sQuery(id+"F15.wireOp",EDGE,"E46.left")])]})});
            fillet(context, id + "F17", {"entities" : qUnion([Q0, Q1]), "radius" : 10 * mm, "tangentPropagation" : true, "allowEdgeOverflow" : false});
        }
        {
            var Q0;
            Q0=makeQuery(id+"F3.boolean.opBoolean","MERGE",FACE,{"derivedFrom":[makeQuery(id+"F1.opExtrude","SWEPT_FACE",FACE,{"disambiguationData":[OSD([sQuery(id+"F0.wireOp",EDGE,"E14.bottom")])]}),makeQuery(id+"F3.opExtrude","SWEPT_FACE",FACE,{"disambiguationData":[OSD([sQuery(id+"F2.wireOp",EDGE,"E19.bottom")])]})]});
            fillet(context, id + "F18", {"entities" : qUnion([Q0]), "radius" : 5 * mm, "tangentPropagation" : true, "allowEdgeOverflow" : false});
        }
        {
            var Q0;
            Q0=makeQuery(id+"F3.boolean.opBoolean","MERGE",FACE,{"derivedFrom":[makeQuery(id+"F1.opExtrude","SWEPT_FACE",FACE,{"disambiguationData":[OSD([sQuery(id+"F0.wireOp",EDGE,"E14.bottom")])]}),makeQuery(id+"F3.opExtrude","SWEPT_FACE",FACE,{"disambiguationData":[OSD([sQuery(id+"F2.wireOp",EDGE,"E19.bottom")])]})]});
            var sketch = newSketch(context, id + "F19", { "sketchPlane" : qUnion([Q0])});
            skPoint(sketch, "E47", {"position": v(-47, 25.05) * mm});
            skPoint(sketch, "E47.positionSnap0", {"position": v(-54, 25.05) * mm});
            skPoint(sketch, "E47.positionSnap1", {"position": v(-47, 50.1) * mm});
            skPoint(sketch, "E48", {"position": v(47, 25.05) * mm});
            skPoint(sketch, "E48.positionSnap0", {"position": v(47, 50.1) * mm});
            skSolve(sketch);
        }
        {
            var Q0;
            Q0=sQuery(id+"F19.wireOp",VERTEX,"E47");
            var Q1;
            Q1=sQuery(id+"F19.wireOp",VERTEX,"E48");
            var Q2;
            Q2=makeQuery(id+"F1.opExtrude","SWEPT_BODY",BODY,{"disambiguationData":[OSD([sQuery(id+"F0.wireOp",EDGE,"E0.bottom"),sQuery(id+"F0.wireOp",EDGE,"E0.top"),sQuery(id+"F0.wireOp",EDGE,"E0.left"),sQuery(id+"F0.wireOp",EDGE,"E0.right"),sQuery(id+"F0.wireOp",EDGE,"E1.MirrorCS"),sQuery(id+"F0.wireOp",EDGE,"E2.MirrorCS"),sQuery(id+"F0.wireOp",EDGE,"E3.MirrorCS"),sQuery(id+"F0.wireOp",EDGE,"E4.MirrorCS"),sQuery(id+"F0.wireOp",EDGE,"E6.MirrorCS"),sQuery(id+"F0.wireOp",EDGE,"E7.MirrorCS"),sQuery(id+"F0.wireOp",EDGE,"E8.MirrorCS"),sQuery(id+"F0.wireOp",EDGE,"E9.MirrorCS"),sQuery(id+"F0.wireOp",EDGE,"E10.MirrorCS"),sQuery(id+"F0.wireOp",EDGE,"E11.MirrorCS"),sQuery(id+"F0.wireOp",EDGE,"E12.MirrorCS"),sQuery(id+"F0.wireOp",EDGE,"E13.MirrorCS"),sQuery(id+"F0.wireOp",EDGE,"E14.bottom"),sQuery(id+"F0.wireOp",EDGE,"E14.top"),sQuery(id+"F0.wireOp",EDGE,"E14.left"),sQuery(id+"F0.wireOp",EDGE,"E14.right"),sQuery(id+"F0.wireOp",EDGE,"E18.0.startCap"),sQuery(id+"F0.wireOp",EDGE,"E18.0.endCap"),sQuery(id+"F0.wireOp",EDGE,"E18.0.left"),sQuery(id+"F0.wireOp",EDGE,"E18.0.right")])]});
            hole(context, id + "F20", {"style" : HoleStyle.C_SINK, "endStyle" : HoleEndStyle.BLIND, "holeDiameter" : 4.2 * mm, "cSinkDiameter" : 8.96 * mm, "cSinkAngle" : 90 * degree, "holeDepth" : 12 * mm, "isTappedThrough" : true, "tappedDepth" : 12 * mm, "tapClearance" : 3, "locations" : qUnion([Q0, Q1]), "scope" : qUnion([Q2])});
        }
    });
